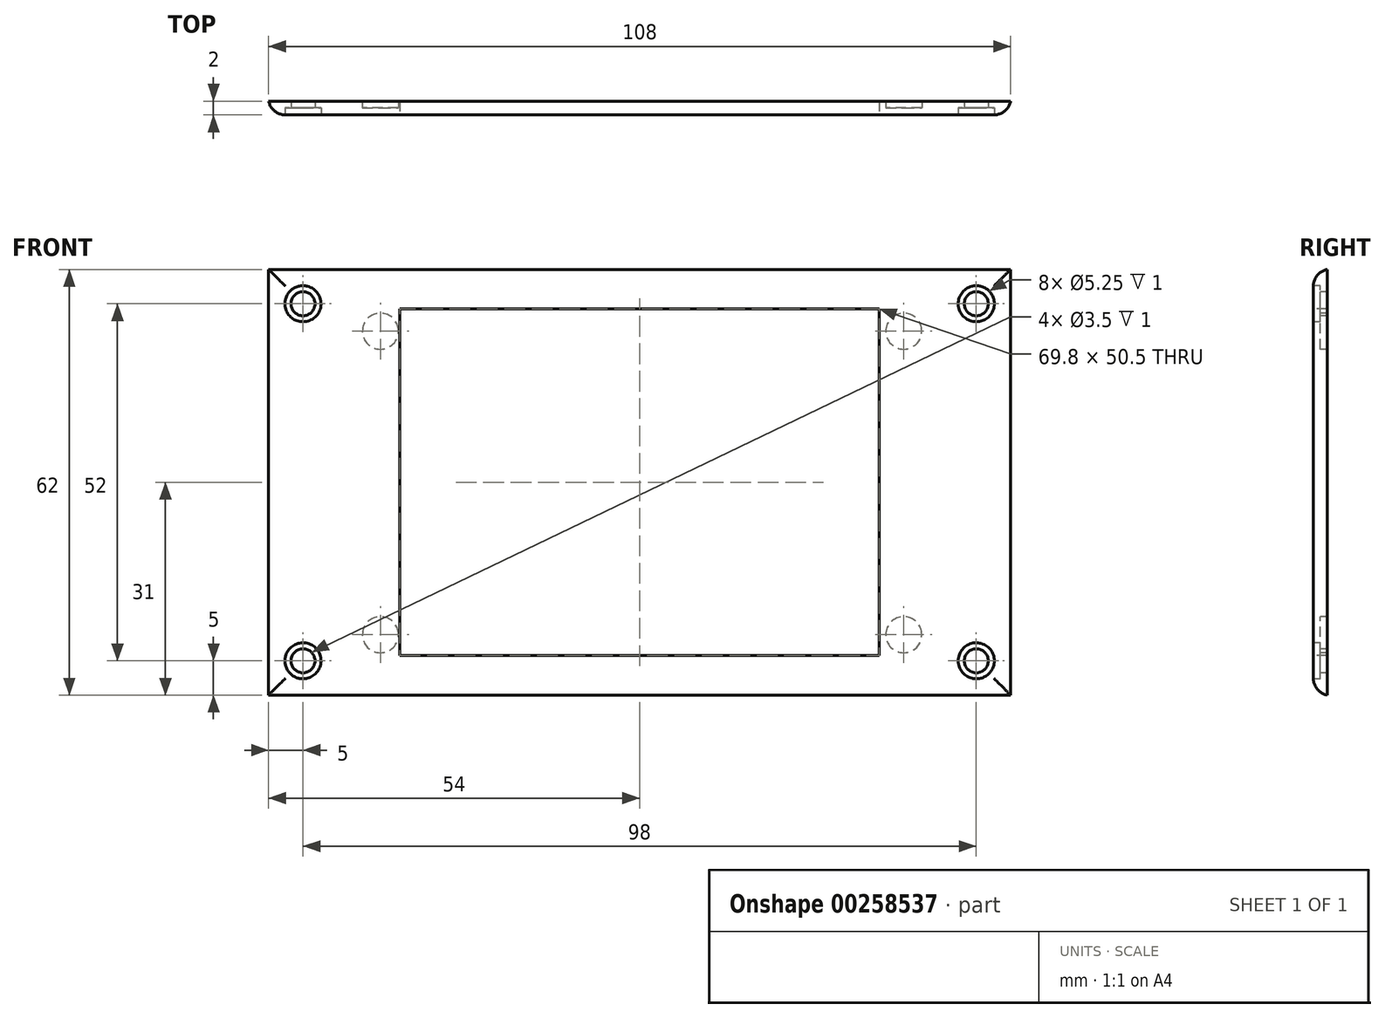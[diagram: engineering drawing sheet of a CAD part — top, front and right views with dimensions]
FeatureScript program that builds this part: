
annotation { "Feature Type Name" : "Feature", "Feature Type Description" : "" }
export const myFeature = defineFeature(function(context is Context, id is Id, definition is map)
    precondition{}
    {
        {
            var Q0;
            Q0=qCreatedBy(makeId("Front.planeOp"),FACE);
            var sketch = newSketch(context, id + "F0", { "sketchPlane" : qUnion([Q0])});
            skLineSegment(sketch, "E0.bottom", {"start": v(-54, 31) * mm, "end": v(54, 31) * mm});
            skLineSegment(sketch, "E0.top", {"start": v(-54, -31) * mm, "end": v(54, -31) * mm});
            skLineSegment(sketch, "E0.left", {"start": v(-54, 31) * mm, "end": v(-54, -31) * mm});
            skLineSegment(sketch, "E0.right", {"start": v(54, 31) * mm, "end": v(54, -31) * mm});
            skPoint(sketch, "E0.middle", {"position": v(0, 0) * mm});
            skSolve(sketch);
        }
        {
            var Q0;
            Q0 = qSketchRegion(id + "F0", true);
            extrude(context, id + "F1", {"entities" : qUnion([Q0]), "oppositeDirection" : true, "depth" : 2 * mm});
        }
        {
            var Q0;
            Q0=qCreatedBy(makeId("Front.planeOp"),FACE);
            var sketch = newSketch(context, id + "F2", { "sketchPlane" : qUnion([Q0])});
            skCircle(sketch, "E1", {"center": v(-49, 26) * mm, "radius": 1.75 * mm});
            skCircle(sketch, "E2", {"center": v(49, 26) * mm, "radius": 1.75 * mm});
            skCircle(sketch, "E3", {"center": v(49, -26) * mm, "radius": 1.75 * mm});
            skCircle(sketch, "E4", {"center": v(-49, -26) * mm, "radius": 1.75 * mm});
            skSolve(sketch);
        }
        {
            var Q0;
            Q0 = qSketchRegion(id + "F2", true);
            extrude(context, id + "F3", {"entities" : qUnion([Q0]), "operationType" : NewBodyOperationType.REMOVE, "endBound" : BoundingType.THROUGH_ALL, "oppositeDirection" : true, "depth" : 25 * mm});
        }
        {
            var Q0;
            Q0=makeQuery(id+"F1.opExtrude","CAP_EDGE",EDGE,{"disambiguationData":[OSD([sQuery(id+"F0.wireOp",EDGE,"E0.left")])],"isStart":true});
            fillet(context, id + "F4", {"entities" : qUnion([Q0]), "radius" : 2.5 * mm, "tangentPropagation" : true, "allowEdgeOverflow" : false});
        }
        {
            var Q0;
            Q0=makeQuery(id+"F1.opExtrude","CAP_EDGE",EDGE,{"disambiguationData":[OSD([sQuery(id+"F0.wireOp",EDGE,"E0.top")])],"isStart":true});
            var Q1;
            Q1=makeQuery(id+"F1.opExtrude","CAP_EDGE",EDGE,{"disambiguationData":[OSD([sQuery(id+"F0.wireOp",EDGE,"E0.bottom")])],"isStart":true});
            var Q2;
            Q2=makeQuery(id+"F1.opExtrude","CAP_EDGE",EDGE,{"disambiguationData":[OSD([sQuery(id+"F0.wireOp",EDGE,"E0.right")])],"isStart":true});
            fillet(context, id + "F5", {"entities" : qUnion([Q0, Q1, Q2]), "radius" : 2.5 * mm, "tangentPropagation" : true, "allowEdgeOverflow" : false});
        }
        {
            var Q0;
            Q0=qCreatedBy(makeId("Front.planeOp"),FACE);
            var sketch = newSketch(context, id + "F6", { "sketchPlane" : qUnion([Q0])});
            skLineSegment(sketch, "E5.bottom", {"start": v(-34.9, 25.25) * mm, "end": v(34.9, 25.25) * mm});
            skLineSegment(sketch, "E5.top", {"start": v(-34.9, -25.25) * mm, "end": v(34.9, -25.25) * mm});
            skLineSegment(sketch, "E5.left", {"start": v(-34.9, 25.25) * mm, "end": v(-34.9, -25.25) * mm});
            skLineSegment(sketch, "E5.right", {"start": v(34.9, 25.25) * mm, "end": v(34.9, -25.25) * mm});
            skSolve(sketch);
        }
        {
            var Q0;
            Q0 = qSketchRegion(id + "F6", true);
            extrude(context, id + "F7", {"entities" : qUnion([Q0]), "operationType" : NewBodyOperationType.REMOVE, "endBound" : BoundingType.THROUGH_ALL, "oppositeDirection" : true, "depth" : 25 * mm});
        }
        {
            var Q0;
            Q0=qCreatedBy(makeId("Front.planeOp"),FACE);
            var sketch = newSketch(context, id + "F8", { "sketchPlane" : qUnion([Q0])});
            skCircle(sketch, "E6", {"center": v(-49, 26) * mm, "radius": 2.62 * mm});
            skCircle(sketch, "E7", {"center": v(49, 26) * mm, "radius": 2.62 * mm});
            skCircle(sketch, "E8", {"center": v(49, -26) * mm, "radius": 2.62 * mm});
            skCircle(sketch, "E9", {"center": v(-49, -26) * mm, "radius": 2.62 * mm});
            skSolve(sketch);
        }
        {
            var Q0;
            Q0 = qSketchRegion(id + "F8", true);
            extrude(context, id + "F9", {"entities" : qUnion([Q0]), "operationType" : NewBodyOperationType.REMOVE, "oppositeDirection" : true, "depth" : 1 * mm});
        }
        {
            var Q0;
            Q0=qCreatedBy(makeId("Front.planeOp"),FACE);
            cPlane(context, id + "F10", {"entities" : qUnion([Q0]), "cplaneType" : CPlaneType.OFFSET, "offset" : 1 * mm, "oppositeDirection" : true, "width" : 150 * mm, "height" : 150 * mm});
        }
        {
            var Q0;
            Q0=qCreatedBy(id+"F10.planeOp",FACE);
            var sketch = newSketch(context, id + "F11", { "sketchPlane" : qUnion([Q0])});
            skLineSegment(sketch, "E10", {"start": v(-34.65, 46.67) * mm, "end": v(34.65, 46.67) * mm, "construction": true});
            skCircle(sketch, "E11", {"center": v(-37.73, 46.67) * mm, "radius": 3 * mm, "construction": true});
            skCircle(sketch, "E12", {"center": v(38.45, 46.67) * mm, "radius": 3 * mm, "construction": true});
            skCircle(sketch, "E13", {"center": v(-37.73, 22) * mm, "radius": 2.62 * mm});
            skCircle(sketch, "E14", {"center": v(-37.73, -22.2) * mm, "radius": 2.62 * mm});
            skCircle(sketch, "E15", {"center": v(38.45, 22) * mm, "radius": 2.62 * mm});
            skCircle(sketch, "E16", {"center": v(38.45, -22.2) * mm, "radius": 2.62 * mm});
            skSolve(sketch);
        }
        {
            var Q0;
            Q0 = qSketchRegion(id + "F11", true);
            extrude(context, id + "F12", {"entities" : qUnion([Q0]), "operationType" : NewBodyOperationType.REMOVE, "endBound" : BoundingType.THROUGH_ALL, "oppositeDirection" : true, "depth" : 25 * mm});
        }
    });
